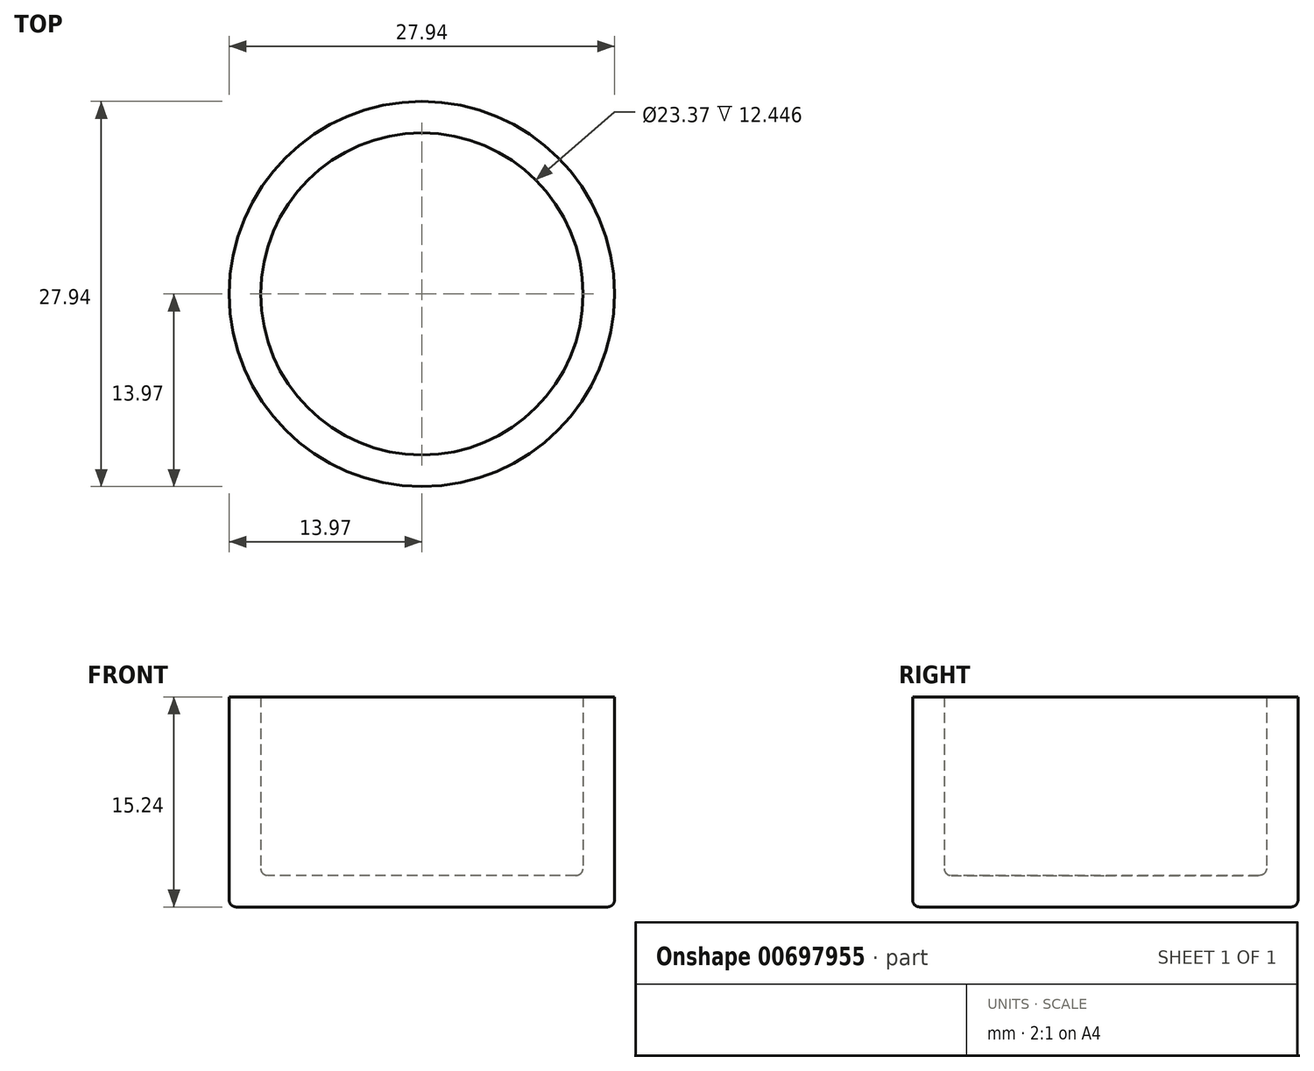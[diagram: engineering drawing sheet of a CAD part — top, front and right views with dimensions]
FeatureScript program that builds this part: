
annotation { "Feature Type Name" : "Feature", "Feature Type Description" : "" }
export const myFeature = defineFeature(function(context is Context, id is Id, definition is map)
    precondition{}
    {
        {
            var Q0;
            Q0=qCreatedBy(makeId("Top.planeOp"),FACE);
            var sketch = newSketch(context, id + "F0", { "sketchPlane" : qUnion([Q0])});
            skCircle(sketch, "E0", {"center": v(0, 0) * mm, "radius": 13.97 * mm});
            skSolve(sketch);
        }
        {
            var Q0;
            Q0=qSketchRegion(id+"F0",true);
            var Q1;
            Q1=makeQuery(id+"F0.imprint","IMPRINT",FACE,{"disambiguationData":[TD([[makeQuery(id+"F0.imprint","IMPRINT",EDGE,{"derivedFrom":sQuery(id+"F0.wireOp",EDGE,"E0")}),1.0]])]});
            extrude(context, id + "F1", {"entities" : qUnion([Q0, Q1]), "depth" : 15.24 * mm, "offsetDistance" : 25.4 * mm});
        }
        {
            var Q0;
            Q0=makeQuery(id+"F1.opExtrude","CAP_FACE",FACE,{"disambiguationData":[OSD([sQuery(id+"F0.wireOp",EDGE,"E0")])],"isStart":false});
            shell(context, id + "F2", {"entities" : qUnion([Q0]), "thickness" : 2.3 * mm});
        }
        {
            var Q0;
            {var subQ0=sQuery(id+"F0.wireOp",EDGE,"E0");Q0=makeQuery(id+"F2.opShell","OFFSET_EDGE",EDGE,{"disambiguationData":[OSD([subQ0]),TDD([makeQuery(id+"F1.opExtrude","CAP_EDGE",EDGE,{"disambiguationData":[OSD([subQ0])],"isStart":true})])]});}
            fillet(context, id + "F3", {"entities" : qUnion([Q0]), "radius" : 0.5 * mm, "tangentPropagation" : true, "allowEdgeOverflow" : false});
        }
        {
            var Q0;
            Q0=makeQuery(id+"F1.opExtrude","CAP_EDGE",EDGE,{"disambiguationData":[OSD([sQuery(id+"F0.wireOp",EDGE,"E0")])],"isStart":true});
            fillet(context, id + "F4", {"entities" : qUnion([Q0]), "radius" : 0.5 * mm, "tangentPropagation" : true, "allowEdgeOverflow" : false});
        }
    });
